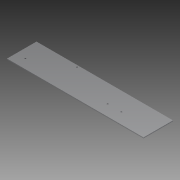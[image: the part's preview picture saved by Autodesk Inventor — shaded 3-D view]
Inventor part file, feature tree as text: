
AUTODESK INVENTOR PART (.ipt)
format: ipt  version: 2013 (Build 170138000, 138)  size: 85,504 bytes
history: native  units: in
note: dims shown in document units (in); Inventor stores cm internally (conversion verified against a paired STEP export)
features: extrude x1, sketch x1
ambient origin geometry x8: Origin, YZ Plane, XZ Plane, XY Plane, X Axis, Y Axis, Z Axis, Center Point
bodies: Solid1 (feature_tree)
feature tree (2):
  extrude  "Extrusion1"  Depth=4.0in
  sketch  "Sketch1"  dims[d0=18.5in d2=4.0in d3=0.2in d5=2.5in d6=1.25in d7=0.25in d8=1.86in d9=0.2in d10=2.5in d11=4.5in d12=0.125in d13=0.0in d16=4.5in]
